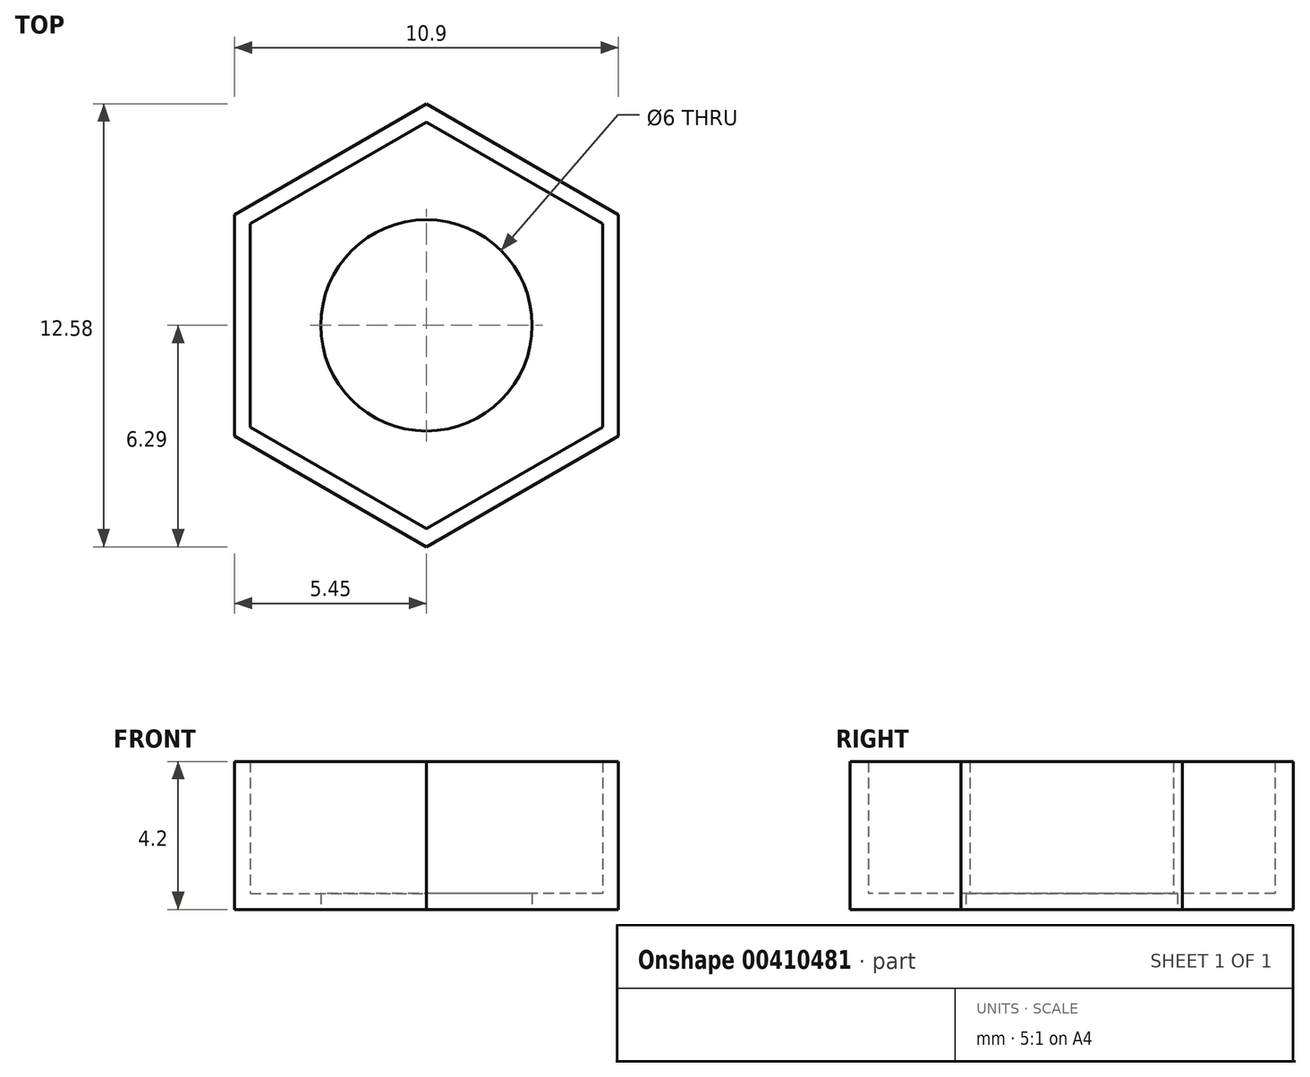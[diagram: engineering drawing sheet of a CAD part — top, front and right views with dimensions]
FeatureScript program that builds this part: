
annotation { "Feature Type Name" : "Feature", "Feature Type Description" : "" }
export const myFeature = defineFeature(function(context is Context, id is Id, definition is map)
    precondition{}
    {
        {
            var Q0;
            Q0=qCreatedBy(makeId("Top.planeOp"),FACE);
            var sketch = newSketch(context, id + "F0", { "sketchPlane" : qUnion([Q0])});
            skCircle(sketch, "E0", {"center": v(0, 0) * mm, "radius": 3 * mm});
            skCircle(sketch, "E1.cCircle", {"center": v(0, 0) * mm, "radius": 5.45 * mm, "construction": true});
            skLineSegment(sketch, "E1.0", {"start": v(5.45, -3.15) * mm, "end": v(0, -6.3) * mm});
            skLineSegment(sketch, "E1.1", {"start": v(0, -6.3) * mm, "end": v(-5.45, -3.15) * mm});
            skLineSegment(sketch, "E1.2", {"start": v(-5.45, -3.15) * mm, "end": v(-5.45, 3.15) * mm});
            skLineSegment(sketch, "E1.3", {"start": v(-5.45, 3.15) * mm, "end": v(0, 6.3) * mm});
            skLineSegment(sketch, "E1.4", {"start": v(0, 6.3) * mm, "end": v(5.45, 3.15) * mm});
            skLineSegment(sketch, "E1.5", {"start": v(5.45, 3.15) * mm, "end": v(5.45, -3.15) * mm});
            skPoint(sketch, "E1.0.midPoint", {"position": v(2.72, -4.72) * mm});
            skSolve(sketch);
        }
        {
            var Q0;
            Q0=makeQuery(id+"F0.imprint","IMPRINT",FACE,{"disambiguationData":[TD([[makeQuery(id+"F0.imprint","IMPRINT",EDGE,{"derivedFrom":sQuery(id+"F0.wireOp",EDGE,"E0")}),1.0]])]});
            var Q1;
            Q1=makeQuery(id+"F0.imprint","IMPRINT",FACE,{"disambiguationData":[TD([[makeQuery(id+"F0.imprint","IMPRINT",EDGE,{"derivedFrom":sQuery(id+"F0.wireOp",EDGE,"E0")}),-1.0]])]});
            extrude(context, id + "F1", {"entities" : qUnion([Q0, Q1]), "depth" : 4.2 * mm, "offsetDistance" : 25 * mm});
        }
        {
            var Q0;
            Q0=makeQuery(id+"F1.opExtrude","CAP_FACE",FACE,{"disambiguationData":[OSD([sQuery(id+"F0.wireOp",EDGE,"E1.0"),sQuery(id+"F0.wireOp",EDGE,"E1.1"),sQuery(id+"F0.wireOp",EDGE,"E1.2"),sQuery(id+"F0.wireOp",EDGE,"E1.3"),sQuery(id+"F0.wireOp",EDGE,"E1.4"),sQuery(id+"F0.wireOp",EDGE,"E1.5")])],"isStart":false});
            shell(context, id + "F2", {"entities" : qUnion([Q0]), "thickness" : 0.45 * mm});
        }
        {
            var Q0;
            Q0=makeQuery(id+"F0.imprint","IMPRINT",FACE,{"disambiguationData":[TD([[makeQuery(id+"F0.imprint","IMPRINT",EDGE,{"derivedFrom":sQuery(id+"F0.wireOp",EDGE,"E0")}),1.0]])]});
            extrude(context, id + "F3", {"entities" : qUnion([Q0]), "operationType" : NewBodyOperationType.REMOVE, "depth" : 0.6 * mm, "offsetDistance" : 25 * mm});
        }
    });
